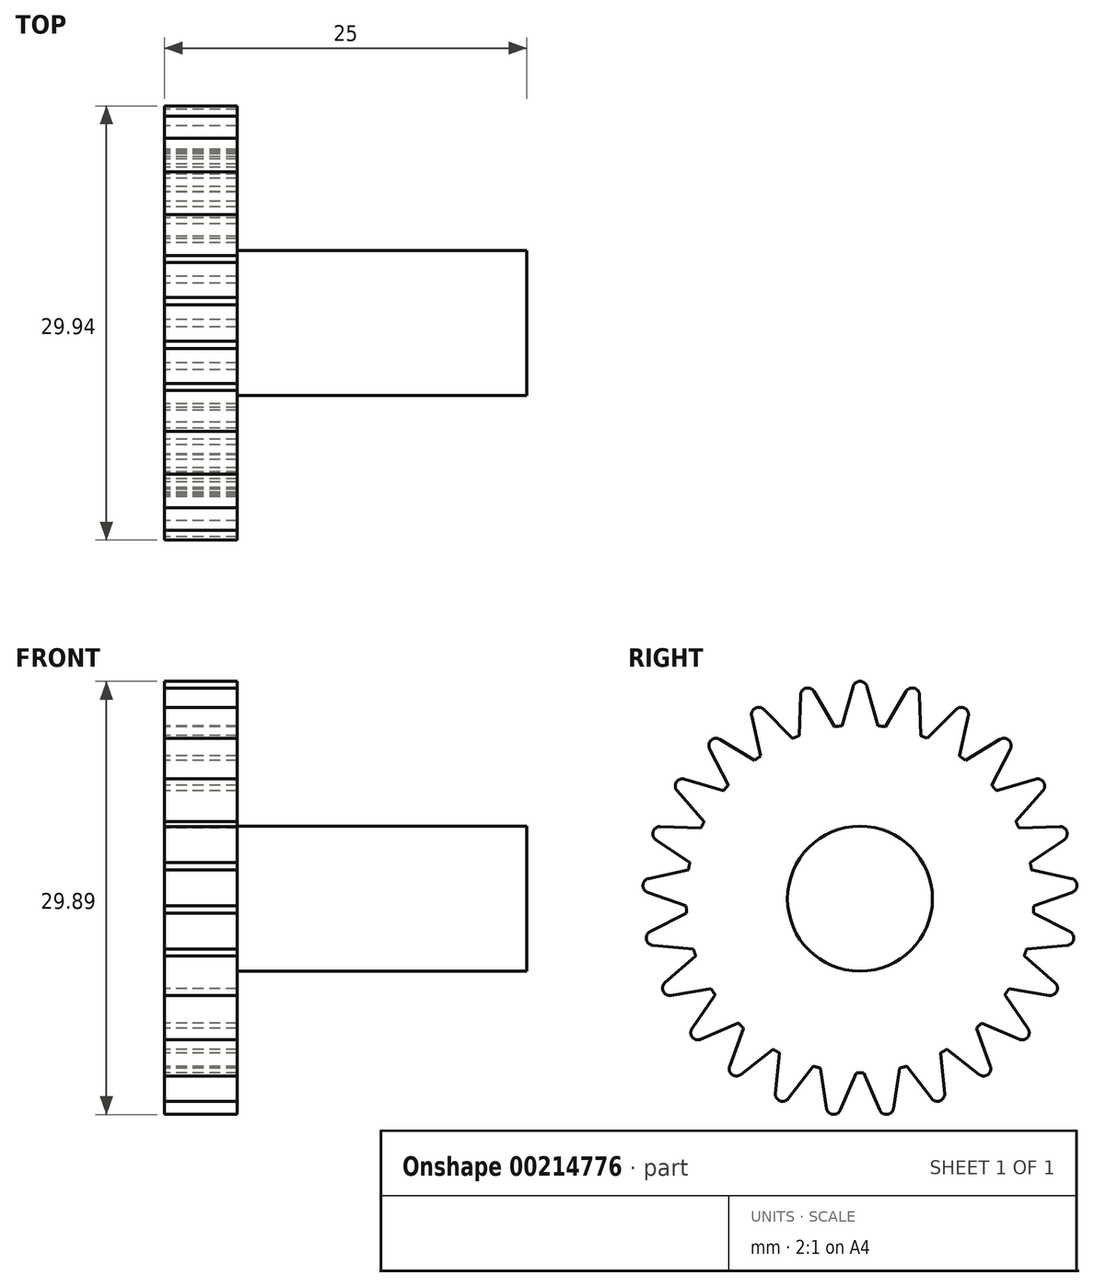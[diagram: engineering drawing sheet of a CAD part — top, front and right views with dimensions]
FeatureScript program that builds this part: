
annotation { "Feature Type Name" : "Feature", "Feature Type Description" : "" }
export const myFeature = defineFeature(function(context is Context, id is Id, definition is map)
    precondition{}
    {
        {
            var Q0;
            Q0=qCreatedBy(makeId("Right.planeOp"),FACE);
            var sketch = newSketch(context, id + "F0", { "sketchPlane" : qUnion([Q0])});
            skArc(sketch, "E0", {"start": v(0.48, 14.64) * mm, "mid": v(0, 15) * mm, "end": v(-0.48, 14.64) * mm});
            skLineSegment(sketch, "E1", {"start": v(-0.48, 14.64) * mm, "end": v(-1.25, 11.93) * mm});
            skLineSegment(sketch, "E2.MirrorCS", {"start": v(0.48, 14.64) * mm, "end": v(1.25, 11.93) * mm});
            skCircle(sketch, "E3", {"center": v(0, 0) * mm, "radius": 12 * mm});
            skLineSegment(sketch, "E4", {"start": v(0, 0) * mm, "end": v(0, 9.86) * mm, "construction": true});
            skLineSegment(sketch, "E5.1.0", {"start": v(-4.1, 14.06) * mm, "end": v(-4.18, 11.25) * mm});
            skArc(sketch, "E5.1.1", {"start": v(-3.17, 14.3) * mm, "mid": v(-3.73, 14.53) * mm, "end": v(-4.1, 14.06) * mm});
            skLineSegment(sketch, "E5.1.2", {"start": v(-3.17, 14.3) * mm, "end": v(-1.76, 11.87) * mm});
            skLineSegment(sketch, "E5.2.0", {"start": v(-7.47, 12.6) * mm, "end": v(-6.85, 9.86) * mm});
            skArc(sketch, "E5.2.1", {"start": v(-6.63, 13.06) * mm, "mid": v(-7.23, 13.14) * mm, "end": v(-7.47, 12.6) * mm});
            skLineSegment(sketch, "E5.2.2", {"start": v(-6.63, 13.06) * mm, "end": v(-4.65, 11.06) * mm});
            skLineSegment(sketch, "E5.3.0", {"start": v(-10.37, 10.34) * mm, "end": v(-9.08, 7.84) * mm});
            skArc(sketch, "E5.3.1", {"start": v(-9.67, 11) * mm, "mid": v(-10.27, 10.93) * mm, "end": v(-10.37, 10.34) * mm});
            skLineSegment(sketch, "E5.3.2", {"start": v(-9.67, 11) * mm, "end": v(-7.26, 9.56) * mm});
            skArc(sketch, "E5.3.3", {"start": v(-9.08, 7.84) * mm, "mid": v(8.21, -8.75) * mm, "end": v(-7.26, 9.56) * mm});
            skLineSegment(sketch, "E5.4.0", {"start": v(-12.62, 7.44) * mm, "end": v(-10.75, 5.34) * mm});
            skArc(sketch, "E5.4.1", {"start": v(-12.1, 8.25) * mm, "mid": v(-12.66, 8.04) * mm, "end": v(-12.62, 7.44) * mm});
            skLineSegment(sketch, "E5.4.2", {"start": v(-12.1, 8.25) * mm, "end": v(-9.4, 7.45) * mm});
            skLineSegment(sketch, "E5.5.0", {"start": v(-14.07, 4.07) * mm, "end": v(-11.74, 2.5) * mm});
            skArc(sketch, "E5.5.1", {"start": v(-13.77, 4.98) * mm, "mid": v(-14.27, 4.64) * mm, "end": v(-14.07, 4.07) * mm});
            skLineSegment(sketch, "E5.5.2", {"start": v(-13.77, 4.98) * mm, "end": v(-10.96, 4.88) * mm});
            skLineSegment(sketch, "E5.6.0", {"start": v(-14.64, 0.44) * mm, "end": v(-11.99, -0.5) * mm});
            skArc(sketch, "E5.6.1", {"start": v(-14.58, 1.4) * mm, "mid": v(-14.97, 0.94) * mm, "end": v(-14.64, 0.44) * mm});
            skLineSegment(sketch, "E5.6.2", {"start": v(-14.58, 1.4) * mm, "end": v(-11.83, 2) * mm});
            skLineSegment(sketch, "E5.7.0", {"start": v(-14.29, -3.22) * mm, "end": v(-11.49, -3.47) * mm});
            skArc(sketch, "E5.7.1", {"start": v(-14.47, -2.27) * mm, "mid": v(-14.73, -2.81) * mm, "end": v(-14.29, -3.22) * mm});
            skLineSegment(sketch, "E5.7.2", {"start": v(-14.47, -2.27) * mm, "end": v(-11.96, -1) * mm});
            skLineSegment(sketch, "E5.8.0", {"start": v(-13.04, -6.67) * mm, "end": v(-10.27, -6.21) * mm});
            skArc(sketch, "E5.8.1", {"start": v(-13.45, -5.8) * mm, "mid": v(-13.57, -6.39) * mm, "end": v(-13.04, -6.67) * mm});
            skLineSegment(sketch, "E5.8.2", {"start": v(-13.45, -5.8) * mm, "end": v(-11.33, -3.95) * mm});
            skLineSegment(sketch, "E5.9.0", {"start": v(-10.97, -9.7) * mm, "end": v(-8.4, -8.57) * mm});
            skArc(sketch, "E5.9.1", {"start": v(-11.58, -8.96) * mm, "mid": v(-11.56, -9.56) * mm, "end": v(-10.97, -9.7) * mm});
            skLineSegment(sketch, "E5.9.2", {"start": v(-11.58, -8.96) * mm, "end": v(-10, -6.64) * mm});
            skLineSegment(sketch, "E5.10.0", {"start": v(-8.21, -12.12) * mm, "end": v(-6, -10.4) * mm});
            skArc(sketch, "E5.10.1", {"start": v(-9, -11.56) * mm, "mid": v(-8.82, -12.14) * mm, "end": v(-8.21, -12.12) * mm});
            skLineSegment(sketch, "E5.10.2", {"start": v(-9, -11.56) * mm, "end": v(-8.03, -8.92) * mm});
            skLineSegment(sketch, "E5.11.0", {"start": v(-4.94, -13.79) * mm, "end": v(-3.23, -11.56) * mm});
            skArc(sketch, "E5.11.1", {"start": v(-5.84, -13.43) * mm, "mid": v(-5.52, -13.95) * mm, "end": v(-4.94, -13.79) * mm});
            skLineSegment(sketch, "E5.11.2", {"start": v(-5.84, -13.43) * mm, "end": v(-5.56, -10.64) * mm});
            skArc(sketch, "E5.11.3", {"start": v(-9.08, 7.84) * mm, "mid": v(8.21, -8.75) * mm, "end": v(-7.26, 9.56) * mm});
            skLineSegment(sketch, "E5.12.0", {"start": v(-1.36, -14.58) * mm, "end": v(-0.25, -12) * mm});
            skArc(sketch, "E5.12.1", {"start": v(-2.31, -14.46) * mm, "mid": v(-1.88, -14.88) * mm, "end": v(-1.36, -14.58) * mm});
            skLineSegment(sketch, "E5.12.2", {"start": v(-2.31, -14.46) * mm, "end": v(-2.74, -11.68) * mm});
            skLineSegment(sketch, "E5.13.0", {"start": v(2.31, -14.46) * mm, "end": v(2.74, -11.68) * mm});
            skArc(sketch, "E5.13.1", {"start": v(1.36, -14.58) * mm, "mid": v(1.88, -14.88) * mm, "end": v(2.31, -14.46) * mm});
            skLineSegment(sketch, "E5.13.2", {"start": v(1.36, -14.58) * mm, "end": v(0.25, -12) * mm});
            skLineSegment(sketch, "E5.14.0", {"start": v(5.84, -13.43) * mm, "end": v(5.56, -10.64) * mm});
            skArc(sketch, "E5.14.1", {"start": v(4.94, -13.79) * mm, "mid": v(5.52, -13.95) * mm, "end": v(5.84, -13.43) * mm});
            skLineSegment(sketch, "E5.14.2", {"start": v(4.94, -13.79) * mm, "end": v(3.23, -11.56) * mm});
            skLineSegment(sketch, "E5.15.0", {"start": v(9, -11.56) * mm, "end": v(8.03, -8.92) * mm});
            skArc(sketch, "E5.15.1", {"start": v(8.21, -12.12) * mm, "mid": v(8.82, -12.14) * mm, "end": v(9, -11.56) * mm});
            skLineSegment(sketch, "E5.15.2", {"start": v(8.21, -12.12) * mm, "end": v(6, -10.4) * mm});
            skArc(sketch, "E5.15.3", {"start": v(-9.08, 7.84) * mm, "mid": v(8.21, -8.75) * mm, "end": v(-7.26, 9.56) * mm});
            skLineSegment(sketch, "E5.16.0", {"start": v(11.58, -8.96) * mm, "end": v(10, -6.64) * mm});
            skArc(sketch, "E5.16.1", {"start": v(10.97, -9.7) * mm, "mid": v(11.56, -9.56) * mm, "end": v(11.58, -8.96) * mm});
            skLineSegment(sketch, "E5.16.2", {"start": v(10.97, -9.7) * mm, "end": v(8.4, -8.57) * mm});
            skLineSegment(sketch, "E5.17.0", {"start": v(13.45, -5.8) * mm, "end": v(11.33, -3.95) * mm});
            skArc(sketch, "E5.17.1", {"start": v(13.04, -6.67) * mm, "mid": v(13.57, -6.39) * mm, "end": v(13.45, -5.8) * mm});
            skLineSegment(sketch, "E5.17.2", {"start": v(13.04, -6.67) * mm, "end": v(10.27, -6.21) * mm});
            skLineSegment(sketch, "E5.18.0", {"start": v(14.47, -2.27) * mm, "end": v(11.96, -1) * mm});
            skArc(sketch, "E5.18.1", {"start": v(14.29, -3.22) * mm, "mid": v(14.73, -2.81) * mm, "end": v(14.47, -2.27) * mm});
            skLineSegment(sketch, "E5.18.2", {"start": v(14.29, -3.22) * mm, "end": v(11.49, -3.47) * mm});
            skLineSegment(sketch, "E5.19.0", {"start": v(14.58, 1.4) * mm, "end": v(11.83, 2) * mm});
            skArc(sketch, "E5.19.1", {"start": v(14.64, 0.44) * mm, "mid": v(14.97, 0.94) * mm, "end": v(14.58, 1.4) * mm});
            skLineSegment(sketch, "E5.19.2", {"start": v(14.64, 0.44) * mm, "end": v(11.99, -0.5) * mm});
            skLineSegment(sketch, "E5.20.0", {"start": v(13.77, 4.98) * mm, "end": v(10.96, 4.88) * mm});
            skArc(sketch, "E5.20.1", {"start": v(14.07, 4.07) * mm, "mid": v(14.27, 4.64) * mm, "end": v(13.77, 4.98) * mm});
            skLineSegment(sketch, "E5.20.2", {"start": v(14.07, 4.07) * mm, "end": v(11.74, 2.5) * mm});
            skLineSegment(sketch, "E5.21.0", {"start": v(12.1, 8.25) * mm, "end": v(9.4, 7.45) * mm});
            skArc(sketch, "E5.21.1", {"start": v(12.62, 7.44) * mm, "mid": v(12.66, 8.04) * mm, "end": v(12.1, 8.25) * mm});
            skLineSegment(sketch, "E5.21.2", {"start": v(12.62, 7.44) * mm, "end": v(10.75, 5.34) * mm});
            skLineSegment(sketch, "E5.22.0", {"start": v(9.67, 11) * mm, "end": v(7.26, 9.56) * mm});
            skArc(sketch, "E5.22.1", {"start": v(10.37, 10.34) * mm, "mid": v(10.27, 10.93) * mm, "end": v(9.67, 11) * mm});
            skLineSegment(sketch, "E5.22.2", {"start": v(10.37, 10.34) * mm, "end": v(9.08, 7.84) * mm});
            skLineSegment(sketch, "E6.2.23.0", {"start": v(6.63, 13.06) * mm, "end": v(4.65, 11.06) * mm});
            skArc(sketch, "E6.3.23.0", {"start": v(7.47, 12.6) * mm, "mid": v(7.23, 13.14) * mm, "end": v(6.63, 13.06) * mm});
            skLineSegment(sketch, "E6.7.23.0", {"start": v(7.47, 12.6) * mm, "end": v(6.85, 9.86) * mm});
            skLineSegment(sketch, "E6.2.24.0", {"start": v(3.17, 14.3) * mm, "end": v(1.76, 11.87) * mm});
            skArc(sketch, "E6.3.24.0", {"start": v(4.1, 14.06) * mm, "mid": v(3.73, 14.53) * mm, "end": v(3.17, 14.3) * mm});
            skLineSegment(sketch, "E6.7.24.0", {"start": v(4.1, 14.06) * mm, "end": v(4.18, 11.25) * mm});
            skSolve(sketch);
        }
        {
            var Q0;
            Q0=qSketchRegion(id+"F0",true);
            extrude(context, id + "F1", {"entities" : qUnion([Q0]), "depth" : 5 * mm});
        }
        {
            var Q0;
            Q0=makeQuery(id+"F1.opExtrude","CAP_FACE",FACE,{"disambiguationData":[OSD([sQuery(id+"F0.wireOp",EDGE,"E0"),sQuery(id+"F0.wireOp",EDGE,"E1"),sQuery(id+"F0.wireOp",EDGE,"E2.MirrorCS"),sQuery(id+"F0.wireOp",EDGE,"E5.1.0"),sQuery(id+"F0.wireOp",EDGE,"E5.1.1"),sQuery(id+"F0.wireOp",EDGE,"E5.1.2"),sQuery(id+"F0.wireOp",EDGE,"E5.2.0"),sQuery(id+"F0.wireOp",EDGE,"E5.2.1"),sQuery(id+"F0.wireOp",EDGE,"E5.2.2"),sQuery(id+"F0.wireOp",EDGE,"E5.3.0"),sQuery(id+"F0.wireOp",EDGE,"E5.3.1"),sQuery(id+"F0.wireOp",EDGE,"E5.3.2"),sQuery(id+"F0.wireOp",EDGE,"E5.4.0"),sQuery(id+"F0.wireOp",EDGE,"E5.4.1"),sQuery(id+"F0.wireOp",EDGE,"E5.4.2"),sQuery(id+"F0.wireOp",EDGE,"E5.5.0"),sQuery(id+"F0.wireOp",EDGE,"E5.5.1"),sQuery(id+"F0.wireOp",EDGE,"E5.5.2"),sQuery(id+"F0.wireOp",EDGE,"E5.6.0"),sQuery(id+"F0.wireOp",EDGE,"E5.6.1"),sQuery(id+"F0.wireOp",EDGE,"E5.6.2"),sQuery(id+"F0.wireOp",EDGE,"E5.7.0"),sQuery(id+"F0.wireOp",EDGE,"E5.7.1"),sQuery(id+"F0.wireOp",EDGE,"E5.7.2"),sQuery(id+"F0.wireOp",EDGE,"E5.8.0"),sQuery(id+"F0.wireOp",EDGE,"E5.8.1"),sQuery(id+"F0.wireOp",EDGE,"E5.8.2"),sQuery(id+"F0.wireOp",EDGE,"E5.9.0"),sQuery(id+"F0.wireOp",EDGE,"E5.9.1"),sQuery(id+"F0.wireOp",EDGE,"E5.9.2"),sQuery(id+"F0.wireOp",EDGE,"E5.10.0"),sQuery(id+"F0.wireOp",EDGE,"E5.10.1"),sQuery(id+"F0.wireOp",EDGE,"E5.10.2"),sQuery(id+"F0.wireOp",EDGE,"E5.11.0"),sQuery(id+"F0.wireOp",EDGE,"E5.11.1"),sQuery(id+"F0.wireOp",EDGE,"E5.11.2"),sQuery(id+"F0.wireOp",EDGE,"E5.12.0"),sQuery(id+"F0.wireOp",EDGE,"E5.12.1"),sQuery(id+"F0.wireOp",EDGE,"E5.12.2"),sQuery(id+"F0.wireOp",EDGE,"E5.13.0"),sQuery(id+"F0.wireOp",EDGE,"E5.13.1"),sQuery(id+"F0.wireOp",EDGE,"E5.13.2"),sQuery(id+"F0.wireOp",EDGE,"E5.14.0"),sQuery(id+"F0.wireOp",EDGE,"E5.14.1"),sQuery(id+"F0.wireOp",EDGE,"E5.14.2"),sQuery(id+"F0.wireOp",EDGE,"E5.15.0"),sQuery(id+"F0.wireOp",EDGE,"E5.15.1"),sQuery(id+"F0.wireOp",EDGE,"E5.15.2"),sQuery(id+"F0.wireOp",EDGE,"E5.16.0"),sQuery(id+"F0.wireOp",EDGE,"E5.16.1"),sQuery(id+"F0.wireOp",EDGE,"E5.16.2"),sQuery(id+"F0.wireOp",EDGE,"E5.17.0"),sQuery(id+"F0.wireOp",EDGE,"E5.17.1"),sQuery(id+"F0.wireOp",EDGE,"E5.17.2"),sQuery(id+"F0.wireOp",EDGE,"E5.18.0"),sQuery(id+"F0.wireOp",EDGE,"E5.18.1"),sQuery(id+"F0.wireOp",EDGE,"E5.18.2"),sQuery(id+"F0.wireOp",EDGE,"E5.19.0"),sQuery(id+"F0.wireOp",EDGE,"E5.19.1"),sQuery(id+"F0.wireOp",EDGE,"E5.19.2"),sQuery(id+"F0.wireOp",EDGE,"E5.20.0"),sQuery(id+"F0.wireOp",EDGE,"E5.20.1"),sQuery(id+"F0.wireOp",EDGE,"E5.20.2"),sQuery(id+"F0.wireOp",EDGE,"E5.21.0"),sQuery(id+"F0.wireOp",EDGE,"E5.21.1"),sQuery(id+"F0.wireOp",EDGE,"E5.21.2"),sQuery(id+"F0.wireOp",EDGE,"E5.22.0"),sQuery(id+"F0.wireOp",EDGE,"E5.22.1"),sQuery(id+"F0.wireOp",EDGE,"E5.22.2"),sQuery(id+"F0.wireOp",EDGE,"E6.2.23.0"),sQuery(id+"F0.wireOp",EDGE,"E6.3.23.0"),sQuery(id+"F0.wireOp",EDGE,"E6.7.23.0"),sQuery(id+"F0.wireOp",EDGE,"E6.2.24.0"),sQuery(id+"F0.wireOp",EDGE,"E6.3.24.0"),sQuery(id+"F0.wireOp",EDGE,"E6.7.24.0"),sQuery(id+"F0.wireOp",EDGE,"E3")])],"isStart":false});
            var sketch = newSketch(context, id + "F2", { "sketchPlane" : qUnion([Q0])});
            skCircle(sketch, "E7", {"center": v(0, 0) * mm, "radius": 5 * mm});
            skSolve(sketch);
        }
        {
            var Q0;
            Q0=makeQuery(id+"F2.imprint","IMPRINT",FACE,{"disambiguationData":[TD([[makeQuery(id+"F2.imprint","IMPRINT",EDGE,{"derivedFrom":sQuery(id+"F2.wireOp",EDGE,"E7")}),1.0]])]});
            extrude(context, id + "F3", {"entities" : qUnion([Q0]), "operationType" : NewBodyOperationType.ADD, "depth" : 20 * mm});
        }
    });
